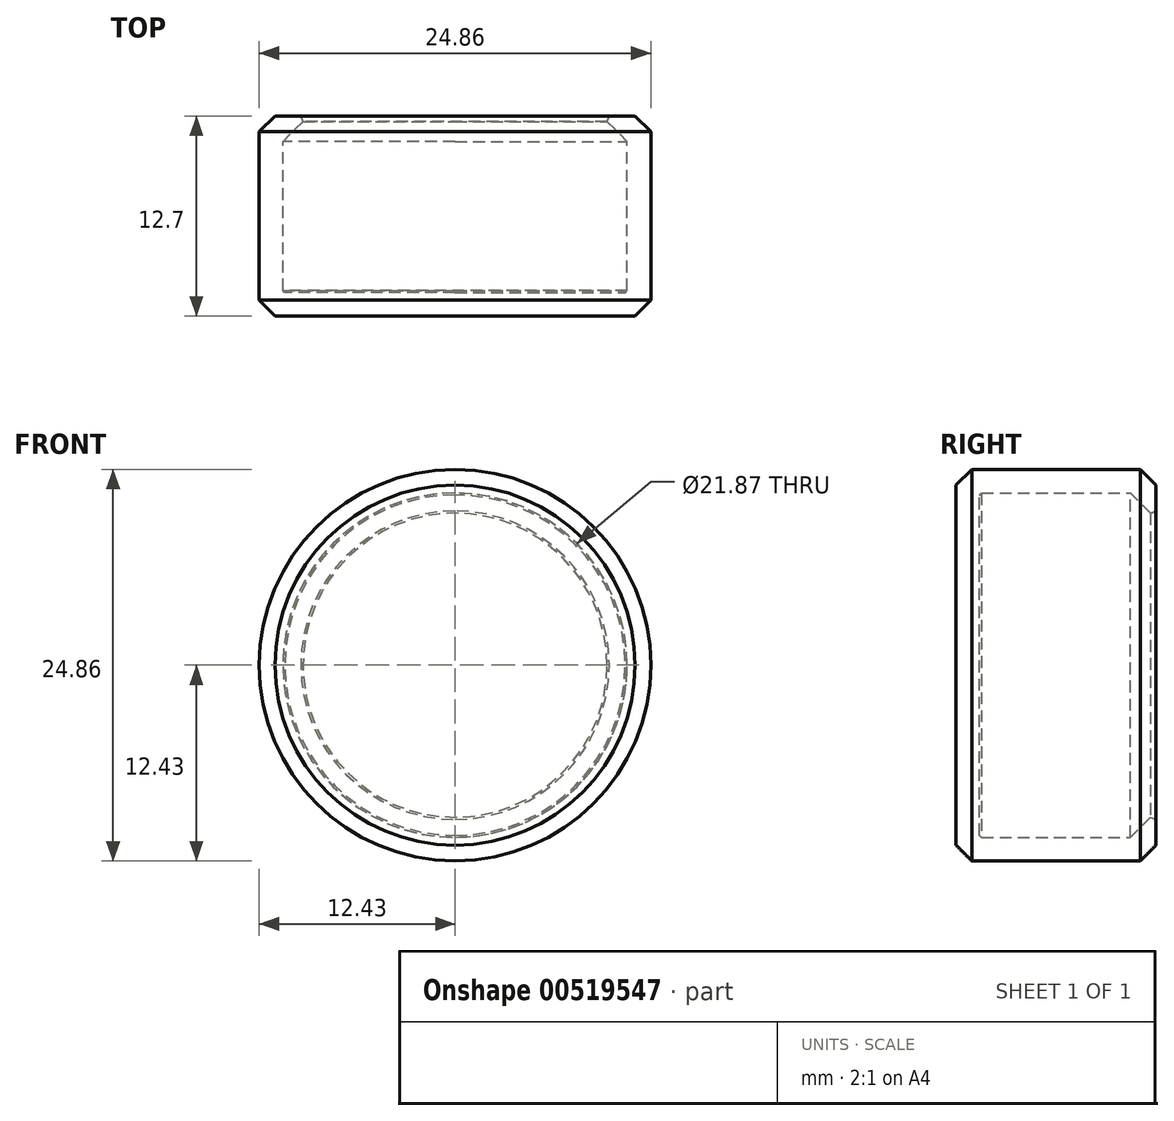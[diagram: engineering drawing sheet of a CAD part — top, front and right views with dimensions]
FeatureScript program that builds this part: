
annotation { "Feature Type Name" : "Feature", "Feature Type Description" : "" }
export const myFeature = defineFeature(function(context is Context, id is Id, definition is map)
    precondition{}
    {
        {
            var Q0;
            Q0=qCreatedBy(makeId("Front.planeOp"),FACE);
            var sketch = newSketch(context, id + "F0", { "sketchPlane" : qUnion([Q0])});
            skCircle(sketch, "E0", {"center": v(0, 0) * mm, "radius": 12.43 * mm});
            skSolve(sketch);
        }
        {
            var Q0;
            Q0=makeQuery(id+"F0.imprint","IMPRINT",FACE,{"disambiguationData":[TD([[makeQuery(id+"F0.imprint","IMPRINT",EDGE,{"derivedFrom":sQuery(id+"F0.wireOp",EDGE,"E0")}),1.0]])]});
            extrude(context, id + "F1", {"entities" : qUnion([Q0]), "depth" : 12.7 * mm, "offsetDistance" : 25 * mm});
        }
        {
            var Q0;
            Q0=makeQuery(id+"F1.opExtrude","CAP_EDGE",EDGE,{"disambiguationData":[OSD([sQuery(id+"F0.wireOp",EDGE,"E0")])],"isStart":true});
            var Q1;
            Q1=makeQuery(id+"F1.opExtrude","SWEPT_FACE",FACE,{"disambiguationData":[OSD([sQuery(id+"F0.wireOp",EDGE,"E0")])]});
            chamfer(context, id + "F2", {"entities" : qUnion([Q0, Q1]), "width" : 1 * mm, "tangentPropagation" : true});
        }
        {
            var Q0;
            Q0=makeQuery(id+"F1.opExtrude","CAP_FACE",FACE,{"disambiguationData":[OSD([sQuery(id+"F0.wireOp",EDGE,"E0")])],"isStart":true});
            shell(context, id + "F3", {"entities" : qUnion([Q0]), "thickness" : 1.5 * mm});
        }
        {
            var Q0;
            Q0=makeQuery(id+"F1.opExtrude","CAP_FACE",FACE,{"disambiguationData":[OSD([sQuery(id+"F0.wireOp",EDGE,"E0")])],"isStart":false});
            cPlane(context, id + "F4", {"entities" : qUnion([Q0]), "cplaneType" : CPlaneType.OFFSET, "offset" : 5 * mm, "oppositeDirection" : true, "width" : 150 * mm, "height" : 150 * mm});
        }
        {
            var Q0;
            {var subQ0=sQuery(id+"F0.wireOp",EDGE,"E0");Q0=makeQuery(id+"F3.opShell","OFFSET_EDGE",EDGE,{"disambiguationData":[OSD([subQ0]),TDD([makeQuery(id+"F2.opChamfer","BLEND_EDGE",EDGE,{"blendedFrom":[makeQuery(id+"F1.opExtrude","CAP_EDGE",EDGE,{"disambiguationData":[OSD([subQ0])],"isStart":true}),makeQuery(id+"F1.opExtrude","CAP_FACE",FACE,{"disambiguationData":[OSD([subQ0])],"isStart":true})],"blendedInto":[makeQuery(id+"F1.opExtrude","CAP_FACE",FACE,{"disambiguationData":[OSD([subQ0])],"isStart":true})]})])]});}
            chamfer(context, id + "F5", {"entities" : qUnion([Q0]), "width" : 0.2 * mm, "tangentPropagation" : true});
        }
        {
            var Q0;
            Q0=qCreatedBy(id+"F4.planeOp",FACE);
            var sketch = newSketch(context, id + "F6", { "sketchPlane" : qUnion([Q0])});
            skCircle(sketch, "E1", {"center": v(0, 0) * mm, "radius": 12.4 * mm});
            skCircle(sketch, "E2.0", {"center": v(0, 0) * mm, "radius": 12.2 * mm});
            skSolve(sketch);
        }
        {
            var Q0;
            Q0=sQuery(id+"F6.wireOp",EDGE,"E2.0");
            extrude(context, id + "F7", {"bodyType" : ToolBodyType.SURFACE, "surfaceEntities" : qUnion([Q0]), "oppositeDirection" : true, "depth" : 1 * mm, "offsetDistance" : 25 * mm});
        }
    });
